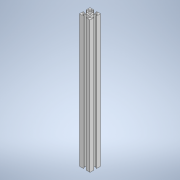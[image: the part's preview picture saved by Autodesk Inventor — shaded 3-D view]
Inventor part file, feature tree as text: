
AUTODESK INVENTOR PART (.ipt)
format: ipt  version: 2022 (Build 260153000, 153)  size: 218,112 bytes
history: native  units: in
note: dims shown in document units (in); Inventor stores cm internally (conversion verified against a paired STEP export)
features: direct_edit x1, extrude x1, sketch x1, projected_geometry x1, move_body x1
ambient origin geometry x8: Origin, YZ Plane, XZ Plane, XY Plane, X Axis, Y Axis, Z Axis, Center Point
bodies: Body1 (feature_tree)
feature tree (5):
  direct_edit  "Direct Edit1"
  extrude  "Extrusion1"  Depth=9.8425in TaperAngle=0.0deg
  sketch  "Sketch1"  dims[d0=0.0in d1=0.0in d2=-0.0394in d3=9.8425in d4=0.0in]
  projected_geometry  "Projected Loop1"
  move_body  "Move1"
